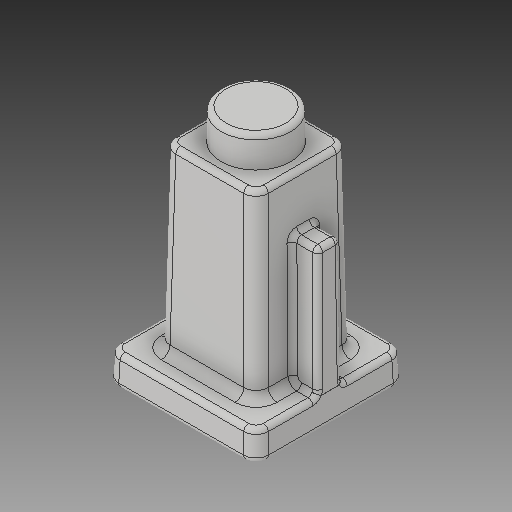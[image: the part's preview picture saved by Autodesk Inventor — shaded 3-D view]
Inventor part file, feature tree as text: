
AUTODESK INVENTOR PART (.ipt)
format: ipt  version: 2019 (Build 230136000, 136)  size: 297,472 bytes
history: native  units: in
note: dims shown in document units (in); Inventor stores cm internally (conversion verified against a paired STEP export)
features: fillet x1
ambient origin geometry x8: Origin, YZ Plane, XZ Plane, XY Plane, X Axis, Y Axis, Z Axis, Center Point
bodies: Solid1 (feature_tree)
feature tree (1):
  fillet  "Fillet5"  [1 undecoded]
note: 1 required parameter value undecoded (feature->parameter linkage not recoverable at this tier; creation-order binding heuristic only, values carry confidence <= 0.55)
